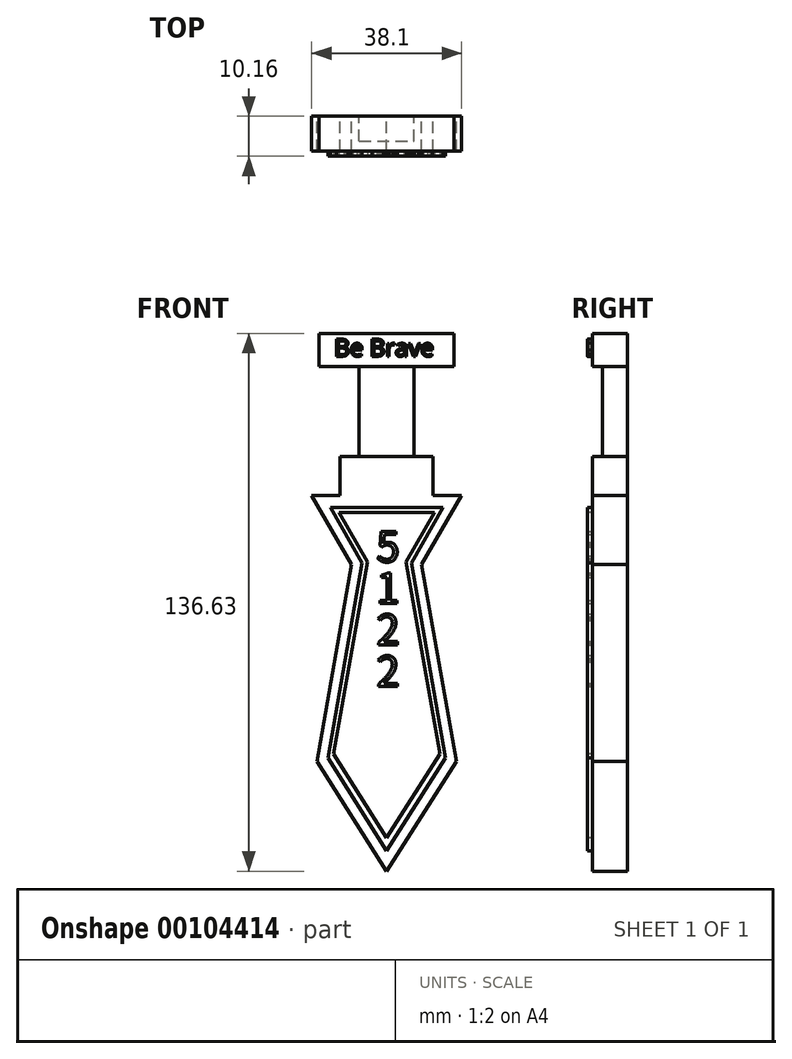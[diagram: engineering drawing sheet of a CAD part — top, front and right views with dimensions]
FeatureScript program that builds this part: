
annotation { "Feature Type Name" : "Feature", "Feature Type Description" : "" }
export const myFeature = defineFeature(function(context is Context, id is Id, definition is map)
    precondition{}
    {
        {
            var Q0;
            Q0=qCreatedBy(makeId("Front.planeOp"),FACE);
            var sketch = newSketch(context, id + "F0", { "sketchPlane" : qUnion([Q0])});
            skLineSegment(sketch, "E0", {"start": v(-22.37, 22.75) * mm, "end": v(15.73, 22.75) * mm});
            skLineSegment(sketch, "E1", {"start": v(15.73, 22.75) * mm, "end": v(5.57, 5.15) * mm});
            skLineSegment(sketch, "E2", {"start": v(-22.37, 22.75) * mm, "end": v(-12.2, 5.15) * mm});
            skLineSegment(sketch, "E3", {"start": v(-12.2, 5.15) * mm, "end": v(-21.03, -44.88) * mm});
            skLineSegment(sketch, "E4", {"start": v(5.57, 5.15) * mm, "end": v(14.4, -44.88) * mm});
            skLineSegment(sketch, "E5", {"start": v(-21.03, -44.88) * mm, "end": v(-3.32, -72.74) * mm});
            skLineSegment(sketch, "E6", {"start": v(-3.32, -72.74) * mm, "end": v(14.4, -44.88) * mm});
            skSolve(sketch);
        }
        {
            var Q0;
            Q0 = qSketchRegion(id + "F0", true);
            var Q1;
            Q1 = qSketchRegion(id + "FieoqVCeBDxOJNk_1", true);
            extrude(context, id + "F1", {"entities" : qUnion([Q0, Q1]), "depth" : 8.9 * mm});
        }
        {
            var Q0;
            Q0=qCreatedBy(makeId("Front.planeOp"),FACE);
            var sketch = newSketch(context, id + "F2", { "sketchPlane" : qUnion([Q0])});
            skLineSegment(sketch, "E7.top", {"start": v(-15.13, 32.64) * mm, "end": v(-10.3, 32.64) * mm});
            skLineSegment(sketch, "E8.left", {"start": v(-10.3, 32.64) * mm, "end": v(-10.3, 55.5) * mm});
            skLineSegment(sketch, "E9.bottom", {"start": v(-20.46, 55.5) * mm, "end": v(-10.3, 55.5) * mm});
            skLineSegment(sketch, "E9.top", {"start": v(-20.46, 63.9) * mm, "end": v(-3.32, 63.9) * mm});
            skLineSegment(sketch, "E9.left", {"start": v(-20.46, 55.5) * mm, "end": v(-20.46, 63.9) * mm});
            skLineSegment(sketch, "E10.0.0", {"start": v(8.5, 22.75) * mm, "end": v(-15.13, 22.75) * mm});
            skLineSegment(sketch, "E10.0.1", {"start": v(-22.37, 22.75) * mm, "end": v(-12.2, 5.15) * mm});
            skLineSegment(sketch, "E10.0.2", {"start": v(-12.2, 5.15) * mm, "end": v(-21.03, -44.88) * mm});
            skLineSegment(sketch, "E10.0.3", {"start": v(-21.03, -44.88) * mm, "end": v(-3.32, -72.74) * mm});
            skLineSegment(sketch, "E10.0.4", {"start": v(-3.32, -72.74) * mm, "end": v(14.4, -44.88) * mm});
            skLineSegment(sketch, "E10.0.5", {"start": v(14.4, -44.88) * mm, "end": v(5.57, 5.15) * mm});
            skLineSegment(sketch, "E10.0.6", {"start": v(5.57, 5.15) * mm, "end": v(15.73, 22.75) * mm});
            skLineSegment(sketch, "E11", {"start": v(-15.13, 32.64) * mm, "end": v(-15.13, 22.75) * mm});
            skLineSegment(sketch, "E12", {"start": v(-3.32, 22.75) * mm, "end": v(-3.32, 72.9) * mm, "construction": true});
            skPoint(sketch, "E12.endSnap0", {"position": v(-3.32, 63.9) * mm});
            skLineSegment(sketch, "E13.MirrorCS", {"start": v(13.83, 63.9) * mm, "end": v(-3.32, 63.9) * mm});
            skLineSegment(sketch, "E14.MirrorCS", {"start": v(13.83, 55.5) * mm, "end": v(13.83, 63.9) * mm});
            skLineSegment(sketch, "E15.MirrorCS", {"start": v(13.83, 55.5) * mm, "end": v(3.67, 55.5) * mm});
            skLineSegment(sketch, "E16.MirrorCS", {"start": v(3.67, 32.64) * mm, "end": v(3.67, 55.5) * mm});
            skLineSegment(sketch, "E17.MirrorCS", {"start": v(8.5, 32.64) * mm, "end": v(8.5, 22.75) * mm});
            skLineSegment(sketch, "E18.MirrorCS", {"start": v(8.5, 32.64) * mm, "end": v(3.67, 32.64) * mm});
            skSolve(sketch);
        }
        {
            var Q0;
            Q0 = qSketchRegion(id + "F2", true);
            extrude(context, id + "F3", {"entities" : qUnion([Q0]), "operationType" : NewBodyOperationType.ADD, "depth" : 8.9 * mm});
        }
        {
            var Q0;
            Q0=makeQuery(id+"F3.boolean.opBoolean","MERGE",FACE,{"derivedFrom":[makeQuery(id+"F1.opExtrude","CAP_FACE",FACE,{"disambiguationData":[OSD([sQuery(id+"F0.wireOp",EDGE,"E0"),sQuery(id+"F0.wireOp",EDGE,"E1"),sQuery(id+"F0.wireOp",EDGE,"E2"),sQuery(id+"F0.wireOp",EDGE,"E3"),sQuery(id+"F0.wireOp",EDGE,"E4"),sQuery(id+"F0.wireOp",EDGE,"E5"),sQuery(id+"F0.wireOp",EDGE,"E6")])],"isStart":false}),makeQuery(id+"F3.opExtrude","CAP_FACE",FACE,{"disambiguationData":[OSD([sQuery(id+"F2.wireOp",EDGE,"E7.top"),sQuery(id+"F2.wireOp",EDGE,"E8.left"),sQuery(id+"F2.wireOp",EDGE,"E9.bottom"),sQuery(id+"F2.wireOp",EDGE,"E9.top"),sQuery(id+"F2.wireOp",EDGE,"E9.left"),sQuery(id+"F2.wireOp",EDGE,"E10.0.0"),sQuery(id+"F2.wireOp",EDGE,"E11"),sQuery(id+"F2.wireOp",EDGE,"E13.MirrorCS"),sQuery(id+"F2.wireOp",EDGE,"E14.MirrorCS"),sQuery(id+"F2.wireOp",EDGE,"E15.MirrorCS"),sQuery(id+"F2.wireOp",EDGE,"E16.MirrorCS"),sQuery(id+"F2.wireOp",EDGE,"E17.MirrorCS"),sQuery(id+"F2.wireOp",EDGE,"E18.MirrorCS")])],"isStart":false})]});
            var sketch = newSketch(context, id + "F4", { "sketchPlane" : qUnion([Q0])});
            skLineSegment(sketch, "E19", {"start": v(-3.32, -72.74) * mm, "end": v(-3.32, 63.9) * mm, "construction": true});
            skLineSegment(sketch, "E20", {"start": v(-17.64, 19.65) * mm, "end": v(-3.32, 19.65) * mm});
            skLineSegment(sketch, "E21", {"start": v(-17.64, 19.65) * mm, "end": v(-9.55, 5.63) * mm});
            skLineSegment(sketch, "E22", {"start": v(-9.55, 5.63) * mm, "end": v(-18.3, -43.98) * mm});
            skLineSegment(sketch, "E23", {"start": v(-18.3, -43.98) * mm, "end": v(-3.32, -67.63) * mm});
            skLineSegment(sketch, "E24.MirrorCS", {"start": v(11, 19.65) * mm, "end": v(-3.32, 19.65) * mm});
            skLineSegment(sketch, "E25.MirrorCS", {"start": v(11, 19.65) * mm, "end": v(2.9, 5.63) * mm});
            skLineSegment(sketch, "E26.MirrorCS", {"start": v(2.9, 5.63) * mm, "end": v(11.65, -43.98) * mm});
            skLineSegment(sketch, "E27.MirrorCS", {"start": v(11.65, -43.98) * mm, "end": v(-3.32, -67.63) * mm});
            skSolve(sketch);
        }
        {
            var Q0;
            Q0 = qSketchRegion(id + "F4", true);
            extrude(context, id + "F5", {"entities" : qUnion([Q0]), "operationType" : NewBodyOperationType.ADD, "depth" : 1.27 * mm});
        }
        {
            var Q0;
            Q0=makeQuery(id+"F5.opExtrude","CAP_FACE",FACE,{"disambiguationData":[OSD([sQuery(id+"F4.wireOp",EDGE,"E20"),sQuery(id+"F4.wireOp",EDGE,"E21"),sQuery(id+"F4.wireOp",EDGE,"E22"),sQuery(id+"F4.wireOp",EDGE,"E23"),sQuery(id+"F4.wireOp",EDGE,"E24.MirrorCS"),sQuery(id+"F4.wireOp",EDGE,"E25.MirrorCS"),sQuery(id+"F4.wireOp",EDGE,"E26.MirrorCS"),sQuery(id+"F4.wireOp",EDGE,"E27.MirrorCS")])],"isStart":false});
            var sketch = newSketch(context, id + "F6", { "sketchPlane" : qUnion([Q0])});
            skLineSegment(sketch, "E28", {"start": v(-15.44, 18.38) * mm, "end": v(-8.2, 5.85) * mm});
            skLineSegment(sketch, "E29", {"start": v(-3.32, 19.65) * mm, "end": v(-3.32, -67.63) * mm, "construction": true});
            skLineSegment(sketch, "E30", {"start": v(-15.44, 18.38) * mm, "end": v(-3.32, 18.38) * mm});
            skLineSegment(sketch, "E31.MirrorCS", {"start": v(8.8, 18.38) * mm, "end": v(-3.32, 18.38) * mm});
            skLineSegment(sketch, "E32.MirrorCS", {"start": v(8.8, 18.38) * mm, "end": v(1.56, 5.85) * mm});
            skLineSegment(sketch, "E33", {"start": v(-8.2, 5.85) * mm, "end": v(-16.8, -42.93) * mm});
            skLineSegment(sketch, "E34", {"start": v(-16.8, -42.93) * mm, "end": v(-3.32, -64.23) * mm});
            skLineSegment(sketch, "E35.MirrorCS", {"start": v(1.56, 5.85) * mm, "end": v(10.16, -42.93) * mm});
            skLineSegment(sketch, "E36.MirrorCS", {"start": v(10.16, -42.93) * mm, "end": v(-3.32, -64.23) * mm});
            skSolve(sketch);
        }
        {
            var Q0;
            Q0 = qSketchRegion(id + "F6", true);
            extrude(context, id + "F7", {"entities" : qUnion([Q0]), "operationType" : NewBodyOperationType.REMOVE, "oppositeDirection" : true, "depth" : 1.27 * mm});
        }
        {
            var Q0;
            Q0=makeQuery(id+"F7.boolean.opBoolean","COPY",FACE,{"derivedFrom":makeQuery(id+"F7.opExtrude","CAP_FACE",FACE,{"disambiguationData":[OSD([sQuery(id+"F6.wireOp",EDGE,"E28"),sQuery(id+"F6.wireOp",EDGE,"E30"),sQuery(id+"F6.wireOp",EDGE,"E31.MirrorCS"),sQuery(id+"F6.wireOp",EDGE,"E32.MirrorCS"),sQuery(id+"F6.wireOp",EDGE,"E33"),sQuery(id+"F6.wireOp",EDGE,"E34"),sQuery(id+"F6.wireOp",EDGE,"E35.MirrorCS"),sQuery(id+"F6.wireOp",EDGE,"E36.MirrorCS")])],"isStart":false})});
            var sketch = newSketch(context, id + "F8", { "sketchPlane" : qUnion([Q0])});
            skText(sketch, "E37", { "text": "5\n1\n2\n2", "fontName": "NotoSansCJKjp-Regular.otf"});
            const initialGuessF8  = {"E37": [-0.00593, 0.00585, 1, 0, 0.0076]};
            skSetInitialGuess(sketch, initialGuessF8);
            skSolve(sketch);
        }
        {
            var Q0;
            Q0 = qSketchRegion(id + "F8", true);
            extrude(context, id + "F9", {"entities" : qUnion([Q0]), "operationType" : NewBodyOperationType.ADD, "depth" : 1.27 * mm});
        }
        {
            var Q0;
            Q0=makeQuery(id+"F3.boolean.opBoolean","MERGE",FACE,{"derivedFrom":[makeQuery(id+"F1.opExtrude","CAP_FACE",FACE,{"disambiguationData":[OSD([sQuery(id+"F0.wireOp",EDGE,"E0"),sQuery(id+"F0.wireOp",EDGE,"E1"),sQuery(id+"F0.wireOp",EDGE,"E2"),sQuery(id+"F0.wireOp",EDGE,"E3"),sQuery(id+"F0.wireOp",EDGE,"E4"),sQuery(id+"F0.wireOp",EDGE,"E5"),sQuery(id+"F0.wireOp",EDGE,"E6")])],"isStart":false}),makeQuery(id+"F3.opExtrude","CAP_FACE",FACE,{"disambiguationData":[OSD([sQuery(id+"F2.wireOp",EDGE,"E7.top"),sQuery(id+"F2.wireOp",EDGE,"E8.left"),sQuery(id+"F2.wireOp",EDGE,"E9.bottom"),sQuery(id+"F2.wireOp",EDGE,"E9.top"),sQuery(id+"F2.wireOp",EDGE,"E9.left"),sQuery(id+"F2.wireOp",EDGE,"E10.0.0"),sQuery(id+"F2.wireOp",EDGE,"E11"),sQuery(id+"F2.wireOp",EDGE,"E13.MirrorCS"),sQuery(id+"F2.wireOp",EDGE,"E14.MirrorCS"),sQuery(id+"F2.wireOp",EDGE,"E15.MirrorCS"),sQuery(id+"F2.wireOp",EDGE,"E16.MirrorCS"),sQuery(id+"F2.wireOp",EDGE,"E17.MirrorCS"),sQuery(id+"F2.wireOp",EDGE,"E18.MirrorCS")])],"isStart":false})]});
            var sketch = newSketch(context, id + "F10", { "sketchPlane" : qUnion([Q0])});
            skText(sketch, "E38", { "text": "Be Brave", "fontName": "OpenSans-Regular.ttf"});
            skPoint(sketch, "E39", {"position": v(8.75, 55.5) * mm});
            const initialGuessF10  = {"E38": [-0.01665, 0.05808, 1, 0, 0.0044]};
            skSetInitialGuess(sketch, initialGuessF10);
            skSolve(sketch);
        }
        {
            var Q0;
            Q0 = qSketchRegion(id + "F10", true);
            extrude(context, id + "F11", {"entities" : qUnion([Q0]), "operationType" : NewBodyOperationType.ADD, "depth" : 1.27 * mm});
        }
        {
            var Q0;
            {var subQ0=sQuery(id+"F2.wireOp",EDGE,"E17.MirrorCS");var subQ1=sQuery(id+"F2.wireOp",EDGE,"E9.left");var subQ2=sQuery(id+"F0.wireOp",EDGE,"E1");var subQ3=sQuery(id+"F0.wireOp",EDGE,"E2");var subQ4=sQuery(id+"F0.wireOp",EDGE,"E5");var subQ5=sQuery(id+"F2.wireOp",EDGE,"E15.MirrorCS");var subQ6=sQuery(id+"F0.wireOp",EDGE,"E0");var subQ7=sQuery(id+"F2.wireOp",EDGE,"E9.bottom");var subQ8=sQuery(id+"F2.wireOp",EDGE,"E18.MirrorCS");var subQ9=sQuery(id+"F2.wireOp",EDGE,"E13.MirrorCS");var subQ10=sQuery(id+"F2.wireOp",EDGE,"E9.top");var subQ11=sQuery(id+"F2.wireOp",EDGE,"E14.MirrorCS");var subQ12=sQuery(id+"F2.wireOp",EDGE,"E11");var subQ13=sQuery(id+"F0.wireOp",EDGE,"E3");var subQ14=sQuery(id+"F2.wireOp",EDGE,"E7.top");var subQ15=sQuery(id+"F2.wireOp",EDGE,"E8.left");var subQ16=sQuery(id+"F0.wireOp",EDGE,"E6");var subQ17=sQuery(id+"F2.wireOp",EDGE,"E16.MirrorCS");var subQ18=sQuery(id+"F0.wireOp",EDGE,"E4");Q0=makeQuery(id+"F11.boolean.opBoolean","SPLIT",FACE,{"disambiguationData":[TD([makeQuery(id+"F1.opExtrude","SWEPT_FACE",FACE,{"disambiguationData":[OSD([subQ6])]})])],"derivedFrom":makeQuery(id+"F3.boolean.opBoolean","MERGE",FACE,{"derivedFrom":[makeQuery(id+"F1.opExtrude","CAP_FACE",FACE,{"disambiguationData":[OSD([subQ6,subQ2,subQ3,subQ13,subQ18,subQ4,subQ16])],"isStart":false}),makeQuery(id+"F3.opExtrude","CAP_FACE",FACE,{"disambiguationData":[OSD([subQ14,subQ15,subQ7,subQ10,subQ1,sQuery(id+"F2.wireOp",EDGE,"E10.0.0"),subQ12,subQ9,subQ11,subQ5,subQ17,subQ0,subQ8])],"isStart":false})]})});}
            var sketch = newSketch(context, id + "F12", { "sketchPlane" : qUnion([Q0])});
            skLineSegment(sketch, "E40.bottom", {"start": v(-10.3, 55.5) * mm, "end": v(3.67, 55.5) * mm});
            skLineSegment(sketch, "E40.top", {"start": v(-10.3, 32.64) * mm, "end": v(3.67, 32.64) * mm});
            skLineSegment(sketch, "E40.left", {"start": v(-10.3, 55.5) * mm, "end": v(-10.3, 32.64) * mm});
            skLineSegment(sketch, "E40.right", {"start": v(3.67, 55.5) * mm, "end": v(3.67, 32.64) * mm});
            skSolve(sketch);
        }
        {
            var Q0;
            Q0 = qSketchRegion(id + "F12", true);
            extrude(context, id + "F13", {"entities" : qUnion([Q0]), "operationType" : NewBodyOperationType.REMOVE, "oppositeDirection" : true, "depth" : 2.54 * mm});
        }
    });
